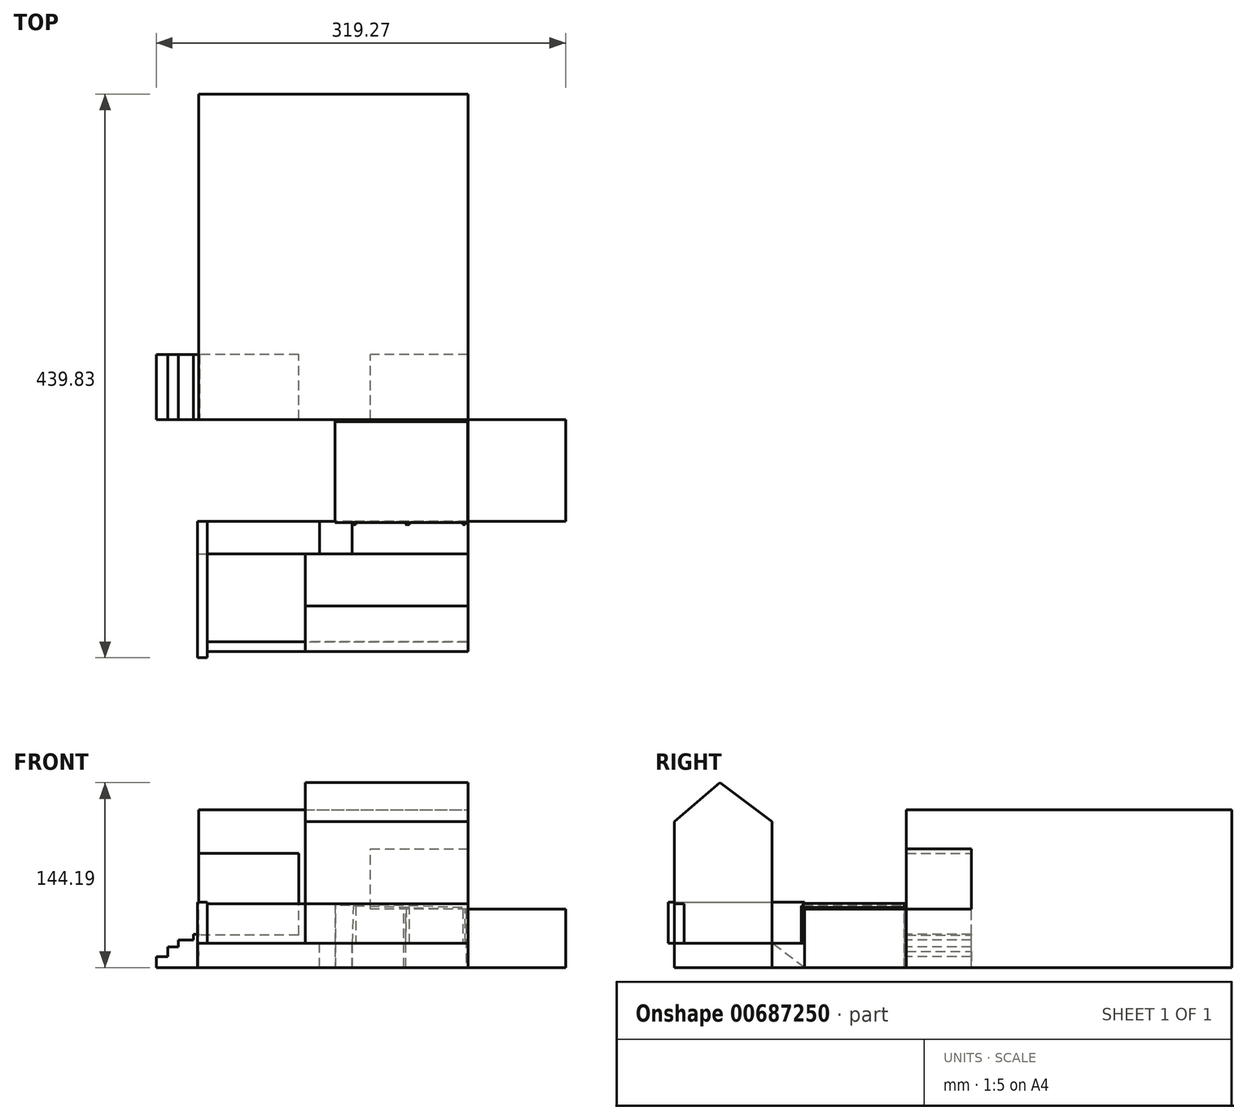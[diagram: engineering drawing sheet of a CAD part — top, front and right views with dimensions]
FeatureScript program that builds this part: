
annotation { "Feature Type Name" : "Feature", "Feature Type Description" : "" }
export const myFeature = defineFeature(function(context is Context, id is Id, definition is map)
    precondition{}
    {
        {
            var Q0;
            Q0=qCreatedBy(makeId("Front.planeOp"),FACE);
            var sketch = newSketch(context, id + "F0", { "sketchPlane" : qUnion([Q0])});
            skLineSegment(sketch, "E0", {"start": v(0, 0) * mm, "end": v(-77.96, 0) * mm});
            skLineSegment(sketch, "E1", {"start": v(0, 0) * mm, "end": v(132.08, 0) * mm});
            skLineSegment(sketch, "E2", {"start": v(132.08, 0) * mm, "end": v(132.08, 45.72) * mm});
            skLineSegment(sketch, "E3", {"start": v(132.08, 45.72) * mm, "end": v(55.88, 45.72) * mm});
            skLineSegment(sketch, "E4", {"start": v(55.88, 45.72) * mm, "end": v(55.88, 92.72) * mm});
            skLineSegment(sketch, "E5", {"start": v(-77.96, 0) * mm, "end": v(-77.96, 25.4) * mm});
            skLineSegment(sketch, "E6", {"start": v(-77.96, 25.4) * mm, "end": v(-14.46, 25.4) * mm});
            skLineSegment(sketch, "E7", {"start": v(0, 25.4) * mm, "end": v(0, 89.23) * mm});
            skLineSegment(sketch, "E8", {"start": v(0, 89.23) * mm, "end": v(-77.96, 89.23) * mm});
            skLineSegment(sketch, "E9", {"start": v(-77.96, 89.23) * mm, "end": v(-77.96, 25.4) * mm});
            skLineSegment(sketch, "E10", {"start": v(-77.96, 89.23) * mm, "end": v(-77.96, 123.01) * mm});
            skLineSegment(sketch, "E11", {"start": v(-24.96, 123.01) * mm, "end": v(132.08, 123.01) * mm});
            skLineSegment(sketch, "E12", {"start": v(132.08, 45.72) * mm, "end": v(132.08, 123.01) * mm});
            skLineSegment(sketch, "E13", {"start": v(55.88, 92.72) * mm, "end": v(132.08, 92.72) * mm});
            skLineSegment(sketch, "E14", {"start": v(0, 25.4) * mm, "end": v(-14.46, 25.4) * mm});
            skLineSegment(sketch, "E15", {"start": v(-77.96, 123.01) * mm, "end": v(-68.6, 123.01) * mm});
            skLineSegment(sketch, "E16", {"start": v(-68.6, 123.01) * mm, "end": v(-24.96, 123.01) * mm});
            skSolve(sketch);
        }
        {
            var Q0;
            Q0=makeQuery(id+"F0.imprint","IMPRINT",FACE,{"disambiguationData":[TD([[makeQuery(id+"F0.imprint","IMPRINT",EDGE,{"derivedFrom":sQuery(id+"F0.wireOp",EDGE,"E0")}),-1.0]])]});
            extrude(context, id + "F1", {"entities" : qUnion([Q0]), "depth" : 254 * mm, "offsetDistance" : 25.4 * mm});
        }
        {
            var Q0;
            Q0=makeQuery(id+"F1.opExtrude","CAP_FACE",FACE,{"disambiguationData":[OSD([sQuery(id+"F0.wireOp",EDGE,"E0"),sQuery(id+"F0.wireOp",EDGE,"E1"),sQuery(id+"F0.wireOp",EDGE,"E2"),sQuery(id+"F0.wireOp",EDGE,"E3"),sQuery(id+"F0.wireOp",EDGE,"E4"),sQuery(id+"F0.wireOp",EDGE,"E5"),sQuery(id+"F0.wireOp",EDGE,"E6"),sQuery(id+"F0.wireOp",EDGE,"E7"),sQuery(id+"F0.wireOp",EDGE,"E8"),sQuery(id+"F0.wireOp",EDGE,"E10"),sQuery(id+"F0.wireOp",EDGE,"E11"),sQuery(id+"F0.wireOp",EDGE,"E12"),sQuery(id+"F0.wireOp",EDGE,"E13"),sQuery(id+"F0.wireOp",EDGE,"E14"),sQuery(id+"F0.wireOp",EDGE,"E15"),sQuery(id+"F0.wireOp",EDGE,"E16")])],"isStart":false});
            var sketch = newSketch(context, id + "F2", { "sketchPlane" : qUnion([Q0])});
            skLineSegment(sketch, "E17", {"start": v(-77.96, 89.23) * mm, "end": v(-77.96, 25.4) * mm});
            skLineSegment(sketch, "E18", {"start": v(-77.96, 25.4) * mm, "end": v(0, 25.4) * mm});
            skLineSegment(sketch, "E19", {"start": v(0, 25.4) * mm, "end": v(0, 89.23) * mm});
            skLineSegment(sketch, "E20", {"start": v(0, 89.23) * mm, "end": v(-77.96, 89.23) * mm});
            skSolve(sketch);
        }
        {
            var Q0;
            Q0=makeQuery(id+"F1.opExtrude","CAP_FACE",FACE,{"disambiguationData":[OSD([sQuery(id+"F0.wireOp",EDGE,"E0"),sQuery(id+"F0.wireOp",EDGE,"E1"),sQuery(id+"F0.wireOp",EDGE,"E2"),sQuery(id+"F0.wireOp",EDGE,"E3"),sQuery(id+"F0.wireOp",EDGE,"E4"),sQuery(id+"F0.wireOp",EDGE,"E5"),sQuery(id+"F0.wireOp",EDGE,"E6"),sQuery(id+"F0.wireOp",EDGE,"E7"),sQuery(id+"F0.wireOp",EDGE,"E8"),sQuery(id+"F0.wireOp",EDGE,"E10"),sQuery(id+"F0.wireOp",EDGE,"E11"),sQuery(id+"F0.wireOp",EDGE,"E12"),sQuery(id+"F0.wireOp",EDGE,"E13"),sQuery(id+"F0.wireOp",EDGE,"E14"),sQuery(id+"F0.wireOp",EDGE,"E15"),sQuery(id+"F0.wireOp",EDGE,"E16")])],"isStart":true});
            var sketch = newSketch(context, id + "F3", { "sketchPlane" : qUnion([Q0])});
            skLineSegment(sketch, "E21", {"start": v(0, 89.23) * mm, "end": v(0, 25.4) * mm});
            skLineSegment(sketch, "E22", {"start": v(0, 25.4) * mm, "end": v(77.96, 25.4) * mm});
            skLineSegment(sketch, "E23", {"start": v(77.96, 25.4) * mm, "end": v(77.96, 89.23) * mm});
            skLineSegment(sketch, "E24", {"start": v(77.96, 89.23) * mm, "end": v(0, 89.23) * mm});
            skLineSegment(sketch, "E25", {"start": v(-132.08, 92.72) * mm, "end": v(-55.88, 92.72) * mm});
            skLineSegment(sketch, "E26", {"start": v(-55.88, 92.72) * mm, "end": v(-55.88, 45.72) * mm});
            skLineSegment(sketch, "E27", {"start": v(-55.88, 45.72) * mm, "end": v(-132.08, 45.72) * mm});
            skLineSegment(sketch, "E28", {"start": v(-132.08, 45.72) * mm, "end": v(-132.08, 92.72) * mm});
            skSolve(sketch);
        }
        {
            var Q0;
            Q0 = qSketchRegion(id + "F3", true);
            extrude(context, id + "F4", {"entities" : qUnion([Q0]), "operationType" : NewBodyOperationType.ADD, "oppositeDirection" : true, "depth" : 203.2 * mm, "offsetDistance" : 25.4 * mm});
        }
        {
            var Q0;
            Q0=makeQuery(id+"F4.boolean.opBoolean","MERGE",FACE,{"derivedFrom":[makeQuery(id+"F1.opExtrude","SWEPT_FACE",FACE,{"disambiguationData":[OSD([sQuery(id+"F0.wireOp",EDGE,"E2")])]}),makeQuery(id+"F1.opExtrude","SWEPT_FACE",FACE,{"disambiguationData":[OSD([sQuery(id+"F0.wireOp",EDGE,"E12")])]}),makeQuery(id+"F4.opExtrude","SWEPT_FACE",FACE,{"disambiguationData":[OSD([sQuery(id+"F3.wireOp",EDGE,"E28")])]})]});
            var sketch = newSketch(context, id + "F5", { "sketchPlane" : qUnion([Q0])});
            skLineSegment(sketch, "E29", {"start": v(-254, 0) * mm, "end": v(-333.28, 0) * mm});
            skLineSegment(sketch, "E30", {"start": v(-333.28, 0) * mm, "end": v(-333.28, 45.72) * mm});
            skLineSegment(sketch, "E31", {"start": v(-333.28, 45.72) * mm, "end": v(-254, 45.72) * mm});
            skLineSegment(sketch, "E32", {"start": v(-254, 45.72) * mm, "end": v(-254, 0) * mm});
            skSolve(sketch);
        }
        {
            var Q0;
            Q0 = qSketchRegion(id + "F5", true);
            extrude(context, id + "F6", {"entities" : qUnion([Q0]), "depth" : 76.2 * mm, "offsetDistance" : 25.4 * mm});
        }
        {
            var Q0;
            Q0=makeQuery(id+"F6.opExtrude","SWEPT_FACE",FACE,{"disambiguationData":[OSD([sQuery(id+"F5.wireOp",EDGE,"E30")])]});
            var sketch = newSketch(context, id + "F7", { "sketchPlane" : qUnion([Q0])});
            skLineSegment(sketch, "E33", {"start": v(132.08, 0) * mm, "end": v(41.74, 0) * mm});
            skLineSegment(sketch, "E34", {"start": v(-78.97, 0) * mm, "end": v(-78.97, 18.9) * mm});
            skLineSegment(sketch, "E35", {"start": v(-78.97, 18.9) * mm, "end": v(16.39, 18.9) * mm});
            skLineSegment(sketch, "E36", {"start": v(132.08, 18.9) * mm, "end": v(132.08, 0) * mm});
            skLineSegment(sketch, "E37", {"start": v(41.74, 18.9) * mm, "end": v(41.74, 0) * mm});
            skLineSegment(sketch, "E38", {"start": v(16.39, 0) * mm, "end": v(16.39, 18.9) * mm});
            skLineSegment(sketch, "E39.trimOffspring", {"start": v(41.74, 18.9) * mm, "end": v(132.08, 18.9) * mm});
            skLineSegment(sketch, "E40.trimOffspring", {"start": v(16.39, 0) * mm, "end": v(-78.97, 0) * mm});
            skSolve(sketch);
        }
        {
            var Q0;
            Q0 = qSketchRegion(id + "F7", true);
            extrude(context, id + "F8", {"entities" : qUnion([Q0]), "depth" : 25.4 * mm, "offsetDistance" : 25.4 * mm});
        }
        {
            var Q0;
            Q0=makeQuery(id+"F8.opExtrude","CAP_FACE",FACE,{"disambiguationData":[OSD([sQuery(id+"F7.wireOp",EDGE,"E34"),sQuery(id+"F7.wireOp",EDGE,"E35"),sQuery(id+"F7.wireOp",EDGE,"E38"),sQuery(id+"F7.wireOp",EDGE,"E40.trimOffspring")])],"isStart":false});
            var sketch = newSketch(context, id + "F9", { "sketchPlane" : qUnion([Q0])});
            skLineSegment(sketch, "E41", {"start": v(-78.97, 18.9) * mm, "end": v(132.06, 18.9) * mm});
            skLineSegment(sketch, "E42", {"start": v(132.06, 18.9) * mm, "end": v(132.06, 0) * mm});
            skLineSegment(sketch, "E43", {"start": v(132.06, 0) * mm, "end": v(-78.97, 0) * mm});
            skLineSegment(sketch, "E44", {"start": v(-78.97, 0) * mm, "end": v(-78.97, 18.9) * mm});
            skSolve(sketch);
        }
        {
            var Q0;
            Q0 = qSketchRegion(id + "F9", true);
            extrude(context, id + "F10", {"entities" : qUnion([Q0]), "depth" : 76.2 * mm, "offsetDistance" : 25.4 * mm});
        }
        {
            var Q0;
            Q0=makeQuery(id+"F8.opExtrude","SWEPT_FACE",FACE,{"disambiguationData":[OSD([sQuery(id+"F7.wireOp",EDGE,"E38")])]});
            var sketch = newSketch(context, id + "F11", { "sketchPlane" : qUnion([Q0])});
            skLineSegment(sketch, "E45", {"start": v(-333.28, 0) * mm, "end": v(-358.68, 18.9) * mm});
            skLineSegment(sketch, "E46", {"start": v(-358.68, 18.9) * mm, "end": v(-358.45, 0) * mm});
            skLineSegment(sketch, "E47", {"start": v(-358.45, 0) * mm, "end": v(-333.28, 0) * mm});
            skSolve(sketch);
        }
        {
            var Q0;
            Q0 = qSketchRegion(id + "F11", true);
            extrude(context, id + "F12", {"entities" : qUnion([Q0]), "depth" : 25.4 * mm, "offsetDistance" : 25.4 * mm});
        }
        {
            var Q0;
            Q0=makeQuery(id+"F2.imprint","IMPRINT",FACE,{"disambiguationData":[TD([[makeQuery(id+"F2.imprint","IMPRINT",EDGE,{"derivedFrom":sQuery(id+"F2.wireOp",EDGE,"E18")}),1.0]])]});
            var sketch = newSketch(context, id + "F13", { "sketchPlane" : qUnion([Q0])});
            skLineSegment(sketch, "E48", {"start": v(-78.38, 0) * mm, "end": v(-110.99, 0) * mm});
            skLineSegment(sketch, "E49", {"start": v(-110.99, 0) * mm, "end": v(-110.99, 8.4) * mm});
            skLineSegment(sketch, "E50", {"start": v(-110.99, 8.4) * mm, "end": v(-102.2, 8.4) * mm});
            skLineSegment(sketch, "E51", {"start": v(-102.2, 8.4) * mm, "end": v(-102.2, 16.2) * mm});
            skLineSegment(sketch, "E52", {"start": v(-102.2, 16.2) * mm, "end": v(-93.87, 16.2) * mm});
            skLineSegment(sketch, "E53", {"start": v(-93.87, 16.2) * mm, "end": v(-93.87, 21.5) * mm});
            skLineSegment(sketch, "E54", {"start": v(-93.87, 21.5) * mm, "end": v(-82.24, 21.5) * mm});
            skLineSegment(sketch, "E55", {"start": v(-82.24, 21.5) * mm, "end": v(-82.24, 25.91) * mm});
            skLineSegment(sketch, "E56", {"start": v(-82.24, 25.91) * mm, "end": v(-77.5, 25.91) * mm});
            skLineSegment(sketch, "E57", {"start": v(-77.5, 25.91) * mm, "end": v(-78.38, 0) * mm});
            skSolve(sketch);
        }
        {
            var Q0;
            Q0 = qSketchRegion(id + "F13", true);
            extrude(context, id + "F14", {"entities" : qUnion([Q0]), "operationType" : NewBodyOperationType.ADD, "oppositeDirection" : true, "depth" : 50.8 * mm, "offsetDistance" : 25.4 * mm});
        }
        {
            var Q0;
            Q0=makeQuery(id+"F2.imprint","IMPRINT",FACE,{"disambiguationData":[TD([[makeQuery(id+"F2.imprint","IMPRINT",EDGE,{"derivedFrom":sQuery(id+"F2.wireOp",EDGE,"E18")}),1.0]])]});
            var sketch = newSketch(context, id + "F15", { "sketchPlane" : qUnion([Q0])});
            skLineSegment(sketch, "E58", {"start": v(28.3, 50.02) * mm, "end": v(28.3, 0) * mm});
            skLineSegment(sketch, "E59", {"start": v(28.3, 0) * mm, "end": v(29.07, 0) * mm});
            skLineSegment(sketch, "E60", {"start": v(29.07, 0) * mm, "end": v(29.07, 50.02) * mm});
            skLineSegment(sketch, "E61", {"start": v(29.07, 50.02) * mm, "end": v(28.3, 50.02) * mm});
            skLineSegment(sketch, "E62", {"start": v(81.93, 0) * mm, "end": v(81.93, 45.58) * mm});
            skLineSegment(sketch, "E63", {"start": v(81.93, 0) * mm, "end": v(83.51, 0) * mm});
            skLineSegment(sketch, "E64", {"start": v(83.51, 0) * mm, "end": v(83.51, 45.58) * mm});
            skLineSegment(sketch, "E65", {"start": v(83.51, 45.58) * mm, "end": v(81.93, 45.58) * mm});
            skLineSegment(sketch, "E66", {"start": v(132.33, 0) * mm, "end": v(132.33, 45.58) * mm});
            skLineSegment(sketch, "E67", {"start": v(132.33, 45.58) * mm, "end": v(130.75, 45.58) * mm});
            skLineSegment(sketch, "E68", {"start": v(130.75, 45.58) * mm, "end": v(130.75, 0) * mm});
            skLineSegment(sketch, "E69", {"start": v(130.75, 0) * mm, "end": v(132.33, 0) * mm});
            skSolve(sketch);
        }
        {
            var Q0;
            Q0=makeQuery(id+"F15.imprint","IMPRINT",FACE,{"disambiguationData":[TD([[makeQuery(id+"F15.imprint","IMPRINT",EDGE,{"derivedFrom":sQuery(id+"F15.wireOp",EDGE,"E58")}),1.0]])]});
            var Q1;
            Q1=makeQuery(id+"F15.imprint","IMPRINT",FACE,{"disambiguationData":[TD([[makeQuery(id+"F15.imprint","IMPRINT",EDGE,{"derivedFrom":sQuery(id+"F15.wireOp",EDGE,"E62")}),-1.0]])]});
            var Q2;
            {var subQ0=sQuery(id+"F15.wireOp",EDGE,"E68");Q2=makeQuery(id+"F15.imprint","IMPRINT",FACE,{"disambiguationData":[TD([[makeQuery(id+"F15.imprint","IMPRINT",EDGE,{"derivedFrom":subQ0}),1.0]])]});}
            extrude(context, id + "F16", {"entities" : qUnion([Q0, Q1, Q2]), "depth" : 1.52 * mm, "offsetDistance" : 25.4 * mm});
        }
        {
            var Q0;
            Q0=makeQuery(id+"F16.opExtrude","CAP_FACE",FACE,{"disambiguationData":[OSD([sQuery(id+"F15.wireOp",EDGE,"E58"),sQuery(id+"F15.wireOp",EDGE,"E59"),sQuery(id+"F15.wireOp",EDGE,"E60"),sQuery(id+"F15.wireOp",EDGE,"E61")])],"isStart":false});
            var sketch = newSketch(context, id + "F17", { "sketchPlane" : qUnion([Q0])});
            skLineSegment(sketch, "E70", {"start": v(28.3, 50.02) * mm, "end": v(131.82, 46.95) * mm});
            skLineSegment(sketch, "E71", {"start": v(131.82, 46.95) * mm, "end": v(131.82, 45.36) * mm});
            skLineSegment(sketch, "E72", {"start": v(131.82, 45.36) * mm, "end": v(28.3, 48.43) * mm});
            skLineSegment(sketch, "E73", {"start": v(28.3, 48.43) * mm, "end": v(28.3, 50.02) * mm});
            skSolve(sketch);
        }
        {
            var Q0;
            Q0 = qSketchRegion(id + "F17", true);
            extrude(context, id + "F18", {"entities" : qUnion([Q0]), "depth" : 78.74 * mm, "offsetDistance" : 25.4 * mm});
        }
        {
            var Q0;
            Q0=makeQuery(id+"F18.opExtrude","CAP_FACE",FACE,{"disambiguationData":[OSD([sQuery(id+"F17.wireOp",EDGE,"E70"),sQuery(id+"F17.wireOp",EDGE,"E71"),sQuery(id+"F17.wireOp",EDGE,"E72"),sQuery(id+"F17.wireOp",EDGE,"E73")])],"isStart":false});
            var sketch = newSketch(context, id + "F19", { "sketchPlane" : qUnion([Q0])});
            skLineSegment(sketch, "E74", {"start": v(41.98, 18.68) * mm, "end": v(42.84, 48) * mm});
            skLineSegment(sketch, "E75", {"start": v(42.84, 48) * mm, "end": v(44.66, 47.94) * mm});
            skLineSegment(sketch, "E76", {"start": v(44.66, 47.94) * mm, "end": v(44.66, 18.66) * mm});
            skLineSegment(sketch, "E77", {"start": v(44.66, 18.66) * mm, "end": v(41.98, 18.68) * mm});
            skLineSegment(sketch, "E78", {"start": v(84.06, 46.78) * mm, "end": v(83.23, 18.68) * mm});
            skLineSegment(sketch, "E79", {"start": v(83.23, 18.68) * mm, "end": v(86.5, 18.58) * mm});
            skLineSegment(sketch, "E80", {"start": v(86.5, 18.58) * mm, "end": v(86.5, 46.95) * mm});
            skLineSegment(sketch, "E81", {"start": v(86.5, 46.95) * mm, "end": v(84.06, 46.78) * mm});
            skLineSegment(sketch, "E82", {"start": v(128.04, 45.47) * mm, "end": v(128.04, 19.02) * mm});
            skLineSegment(sketch, "E83", {"start": v(128.04, 19.02) * mm, "end": v(130.04, 19.02) * mm});
            skLineSegment(sketch, "E84", {"start": v(130.04, 19.02) * mm, "end": v(130.04, 45.36) * mm});
            skLineSegment(sketch, "E85", {"start": v(130.04, 45.36) * mm, "end": v(128.04, 45.47) * mm});
            skSolve(sketch);
        }
        {
            var Q0;
            Q0 = qSketchRegion(id + "F19", true);
            extrude(context, id + "F20", {"entities" : qUnion([Q0]), "depth" : 1.52 * mm, "offsetDistance" : 25.4 * mm});
        }
        {
            var Q0;
            Q0=makeQuery(id+"F8.opExtrude","SWEPT_FACE",FACE,{"disambiguationData":[OSD([sQuery(id+"F7.wireOp",EDGE,"E34")])]});
            var sketch = newSketch(context, id + "F21", { "sketchPlane" : qUnion([Q0])});
            skLineSegment(sketch, "E86", {"start": v(333.28, 18.9) * mm, "end": v(439.83, 18.9) * mm});
            skLineSegment(sketch, "E87", {"start": v(439.83, 18.9) * mm, "end": v(439.83, 51.07) * mm});
            skLineSegment(sketch, "E88", {"start": v(439.83, 51.07) * mm, "end": v(333.28, 51.07) * mm});
            skLineSegment(sketch, "E89", {"start": v(333.28, 51.07) * mm, "end": v(333.28, 18.9) * mm});
            skSolve(sketch);
        }
        {
            var Q0;
            Q0 = qSketchRegion(id + "F21", true);
            extrude(context, id + "F22", {"entities" : qUnion([Q0]), "oppositeDirection" : true, "depth" : 7.62 * mm, "offsetDistance" : 25.4 * mm});
        }
        {
            var Q0;
            Q0=makeQuery(id+"F10.opExtrude","CAP_FACE",FACE,{"disambiguationData":[OSD([sQuery(id+"F9.wireOp",EDGE,"E41"),sQuery(id+"F9.wireOp",EDGE,"E42"),sQuery(id+"F9.wireOp",EDGE,"E43"),sQuery(id+"F9.wireOp",EDGE,"E44")])],"isStart":false});
            var sketch = newSketch(context, id + "F23", { "sketchPlane" : qUnion([Q0])});
            skLineSegment(sketch, "E90", {"start": v(132.06, 18.9) * mm, "end": v(132.06, 49.86) * mm});
            skLineSegment(sketch, "E91", {"start": v(132.06, 49.86) * mm, "end": v(-72, 49.86) * mm});
            skLineSegment(sketch, "E92", {"start": v(-72, 49.86) * mm, "end": v(-72, 18.9) * mm});
            skLineSegment(sketch, "E93", {"start": v(-72, 18.9) * mm, "end": v(132.06, 18.9) * mm});
            skSolve(sketch);
        }
        {
            var Q0;
            Q0 = qSketchRegion(id + "F23", true);
            extrude(context, id + "F24", {"entities" : qUnion([Q0]), "oppositeDirection" : true, "depth" : 7.62 * mm, "offsetDistance" : 25.4 * mm});
        }
        {
            var Q0;
            Q0=makeQuery(id+"F10.opExtrude","SWEPT_FACE",FACE,{"disambiguationData":[OSD([sQuery(id+"F9.wireOp",EDGE,"E42")])]});
            var sketch = newSketch(context, id + "F25", { "sketchPlane" : qUnion([Q0])});
            skLineSegment(sketch, "E94", {"start": v(-358.68, 18.9) * mm, "end": v(-358.68, 49.4) * mm});
            skLineSegment(sketch, "E95", {"start": v(-358.68, 113.91) * mm, "end": v(-434.88, 113.91) * mm});
            skLineSegment(sketch, "E96", {"start": v(-434.88, 113.91) * mm, "end": v(-434.88, 18.9) * mm});
            skLineSegment(sketch, "E97", {"start": v(-434.88, 18.9) * mm, "end": v(-358.68, 18.9) * mm});
            skLineSegment(sketch, "E98", {"start": v(-358.68, 113.91) * mm, "end": v(-358.68, 49.4) * mm});
            skLineSegment(sketch, "E99", {"start": v(-434.88, 113.91) * mm, "end": v(-399.24, 144.2) * mm});
            skLineSegment(sketch, "E100", {"start": v(-399.24, 144.2) * mm, "end": v(-358.68, 113.91) * mm});
            skSolve(sketch);
        }
        {
            var Q0;
            Q0 = qSketchRegion(id + "F25", true);
            extrude(context, id + "F26", {"entities" : qUnion([Q0]), "oppositeDirection" : true, "depth" : 127 * mm, "offsetDistance" : 25.4 * mm});
        }
    });
